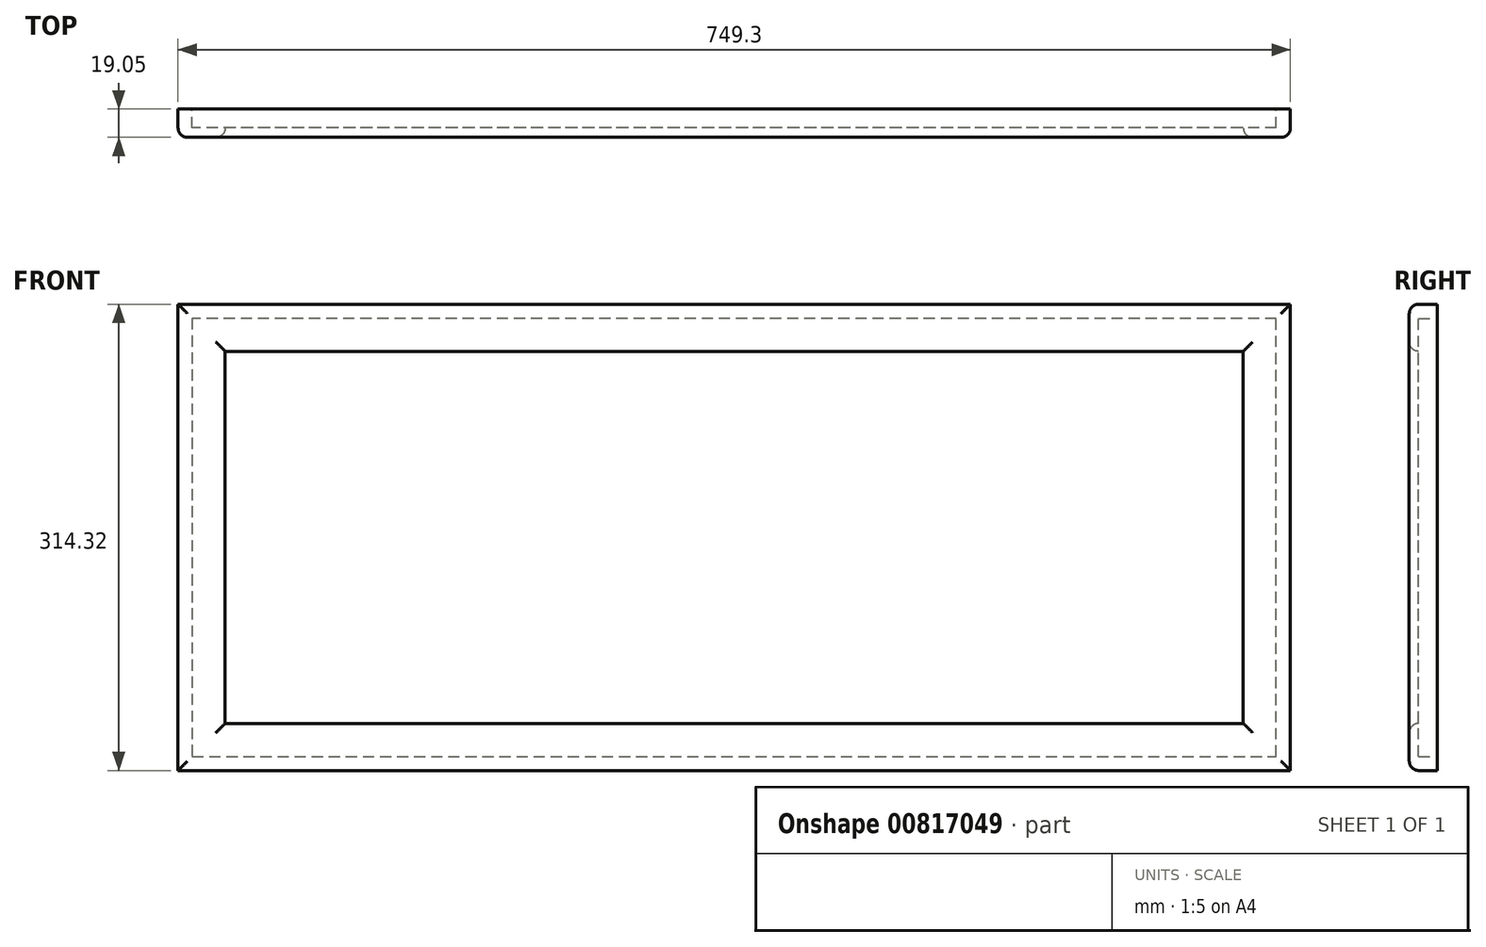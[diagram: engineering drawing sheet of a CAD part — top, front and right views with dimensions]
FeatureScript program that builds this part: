
annotation { "Feature Type Name" : "Feature", "Feature Type Description" : "" }
export const myFeature = defineFeature(function(context is Context, id is Id, definition is map)
    precondition{}
    {
        {
            var Q0;
            Q0=qCreatedBy(makeId("Front.planeOp"),FACE);
            var sketch = newSketch(context, id + "F0", { "sketchPlane" : qUnion([Q0])});
            skLineSegment(sketch, "E0.bottom", {"start": v(365.13, 147.64) * mm, "end": v(-365.13, 147.64) * mm});
            skLineSegment(sketch, "E0.top", {"start": v(365.13, -147.64) * mm, "end": v(-365.13, -147.64) * mm});
            skLineSegment(sketch, "E0.left", {"start": v(365.13, 147.64) * mm, "end": v(365.13, -147.64) * mm});
            skLineSegment(sketch, "E0.right", {"start": v(-365.13, 147.64) * mm, "end": v(-365.13, -147.64) * mm});
            skPoint(sketch, "E0.middle", {"position": v(0, 0) * mm});
            skSolve(sketch);
        }
        {
            var Q0;
            Q0 = qSketchRegion(id + "F0", true);
            extrude(context, id + "F1", {"entities" : qUnion([Q0]), "depth" : 12.7 * mm, "offsetDistance" : 25.4 * mm});
        }
        {
            var Q0;
            Q0=makeQuery(id+"F1.opExtrude","SWEPT_FACE",FACE,{"disambiguationData":[OSD([sQuery(id+"F0.wireOp",EDGE,"E0.left")])]});
            var sketch = newSketch(context, id + "F2", { "sketchPlane" : qUnion([Q0])});
            skLineSegment(sketch, "E1", {"start": v(0, 147.64) * mm, "end": v(0, 157.16) * mm});
            skLineSegment(sketch, "E2", {"start": v(0, 157.16) * mm, "end": v(-12.7, 157.16) * mm});
            skLineSegment(sketch, "E3", {"start": v(-19.05, 150.81) * mm, "end": v(-19.05, 131.76) * mm});
            skLineSegment(sketch, "E4", {"start": v(-12.7, 125.41) * mm, "end": v(-12.7, 125.41) * mm});
            skLineSegment(sketch, "E5", {"start": v(-12.7, 125.41) * mm, "end": v(-12.7, 147.64) * mm});
            skLineSegment(sketch, "E6", {"start": v(-12.7, 147.64) * mm, "end": v(0, 147.64) * mm});
            skPoint(sketch, "E7.visualSharp", {"position": v(-19.05, 157.16) * mm});
            skArc(sketch, "E7.filletArc", {"start": v(-12.7, 157.16) * mm, "mid": v(-17.2, 155.3) * mm, "end": v(-19.05, 150.81) * mm});
            skPoint(sketch, "E8.visualSharp", {"position": v(-19.05, 125.41) * mm});
            skArc(sketch, "E8.filletArc", {"start": v(-19.05, 131.76) * mm, "mid": v(-17.2, 127.27) * mm, "end": v(-12.7, 125.41) * mm});
            skSolve(sketch);
        }
        {
            var Q0;
            Q0=makeQuery(id+"F2.imprint","IMPRINT",FACE,{"disambiguationData":[TD([[makeQuery(id+"F2.imprint","IMPRINT",EDGE,{"derivedFrom":sQuery(id+"F2.wireOp",EDGE,"E1")}),1.0]])]});
            var Q1;
            Q1=makeQuery(id+"F1.opExtrude","CAP_EDGE",EDGE,{"disambiguationData":[OSD([sQuery(id+"F0.wireOp",EDGE,"E0.bottom")])],"isStart":false});
            var Q2;
            Q2=makeQuery(id+"F1.opExtrude","CAP_EDGE",EDGE,{"disambiguationData":[OSD([sQuery(id+"F0.wireOp",EDGE,"E0.right")])],"isStart":false});
            var Q3;
            Q3=makeQuery(id+"F1.opExtrude","CAP_EDGE",EDGE,{"disambiguationData":[OSD([sQuery(id+"F0.wireOp",EDGE,"E0.top")])],"isStart":false});
            var Q4;
            Q4=makeQuery(id+"F1.opExtrude","CAP_EDGE",EDGE,{"disambiguationData":[OSD([sQuery(id+"F0.wireOp",EDGE,"E0.left")])],"isStart":false});
            sweep(context, id + "F3", {"profiles" : qUnion([Q0]), "path" : qUnion([Q1, Q2, Q3, Q4])});
        }
    });
